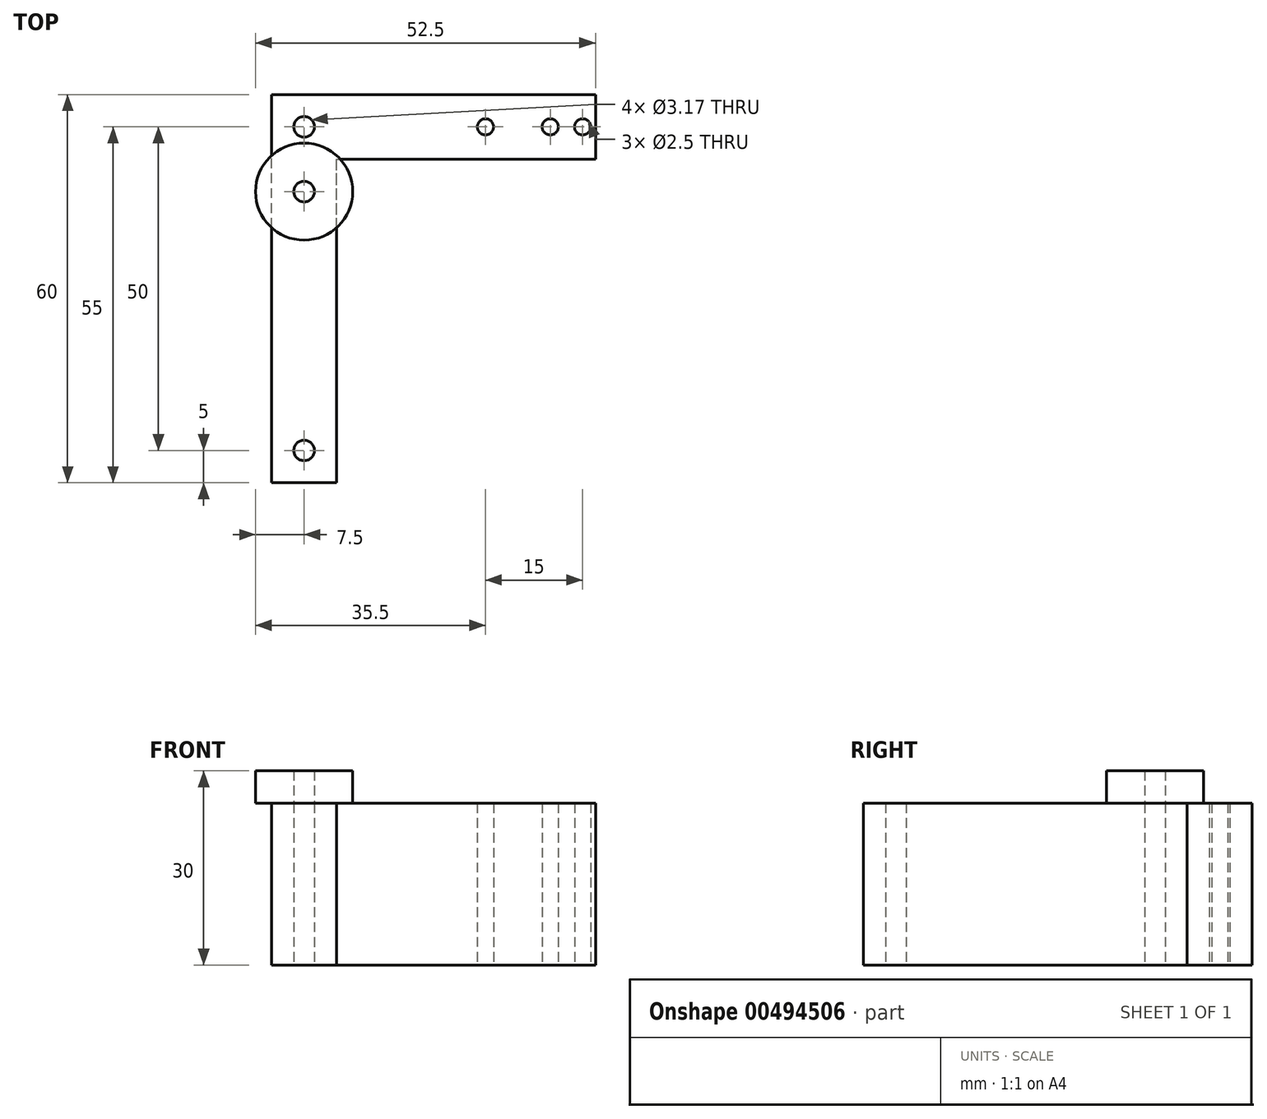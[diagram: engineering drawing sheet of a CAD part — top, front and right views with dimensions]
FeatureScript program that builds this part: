
annotation { "Feature Type Name" : "Feature", "Feature Type Description" : "" }
export const myFeature = defineFeature(function(context is Context, id is Id, definition is map)
    precondition{}
    {
        {
            var Q0;
            Q0=qCreatedBy(makeId("Top.planeOp"),FACE);
            var sketch = newSketch(context, id + "F0", { "sketchPlane" : qUnion([Q0])});
            skLineSegment(sketch, "E0.bottom", {"start": v(5, -30) * mm, "end": v(-5, -30) * mm});
            skLineSegment(sketch, "E0.top", {"start": v(5, 30) * mm, "end": v(-5, 30) * mm});
            skLineSegment(sketch, "E0.left", {"start": v(5, -30) * mm, "end": v(5, 30) * mm});
            skLineSegment(sketch, "E0.right", {"start": v(-5, -30) * mm, "end": v(-5, 30) * mm});
            skPoint(sketch, "E0.middle", {"position": v(0, 0) * mm});
            skCircle(sketch, "E1", {"center": v(0, 15) * mm, "radius": 1.59 * mm});
            skLineSegment(sketch, "E2.left", {"start": v(5, 0) * mm, "end": v(5, 30) * mm});
            skCircle(sketch, "E3", {"center": v(0, -25) * mm, "radius": 1.59 * mm});
            skCircle(sketch, "E4", {"center": v(0, 25) * mm, "radius": 1.59 * mm});
            skLineSegment(sketch, "E5.bottom", {"start": v(5, 30) * mm, "end": v(45, 30) * mm});
            skLineSegment(sketch, "E5.top", {"start": v(5, 20) * mm, "end": v(45, 20) * mm});
            skLineSegment(sketch, "E5.left", {"start": v(5, 30) * mm, "end": v(5, 20) * mm});
            skLineSegment(sketch, "E5.right", {"start": v(45, 30) * mm, "end": v(45, 20) * mm});
            skCircle(sketch, "E6", {"center": v(43, 25) * mm, "radius": 1.25 * mm});
            skPoint(sketch, "E6.centerSnap0", {"position": v(45, 25) * mm});
            skCircle(sketch, "E7", {"center": v(28, 25) * mm, "radius": 1.25 * mm});
            skCircle(sketch, "E8", {"center": v(38, 25) * mm, "radius": 1.25 * mm});
            skSolve(sketch);
        }
        {
            var Q0;
            Q0=makeQuery(id+"F0.imprint","IMPRINT",FACE,{"disambiguationData":[TD([[makeQuery(id+"F0.imprint","IMPRINT",EDGE,{"derivedFrom":sQuery(id+"F0.wireOp",EDGE,"E0.bottom")}),-1.0]])]});
            var Q1;
            Q1=makeQuery(id+"F0.imprint","IMPRINT",FACE,{"disambiguationData":[TD([[makeQuery(id+"F0.imprint","IMPRINT",EDGE,{"derivedFrom":sQuery(id+"F0.wireOp",EDGE,"E5.bottom")}),-1.0]])]});
            extrude(context, id + "F1", {"entities" : qUnion([Q0, Q1]), "depth" : 25 * mm, "offsetDistance" : 25 * mm});
        }
        {
            var Q0;
            Q0=makeQuery(id+"F1.opExtrude","CAP_FACE",FACE,{"disambiguationData":[OSD([sQuery(id+"F0.wireOp",EDGE,"E0.bottom"),sQuery(id+"F0.wireOp",EDGE,"E0.top"),sQuery(id+"F0.wireOp",EDGE,"E0.left"),sQuery(id+"F0.wireOp",EDGE,"E0.right"),sQuery(id+"F0.wireOp",EDGE,"E1"),sQuery(id+"F0.wireOp",EDGE,"E2.left"),sQuery(id+"F0.wireOp",EDGE,"E3"),sQuery(id+"F0.wireOp",EDGE,"E4"),sQuery(id+"F0.wireOp",EDGE,"E5.bottom"),sQuery(id+"F0.wireOp",EDGE,"E5.top"),sQuery(id+"F0.wireOp",EDGE,"E5.right"),sQuery(id+"F0.wireOp",EDGE,"E6"),sQuery(id+"F0.wireOp",EDGE,"E7"),sQuery(id+"F0.wireOp",EDGE,"E8")])],"isStart":false});
            var sketch = newSketch(context, id + "F2", { "sketchPlane" : qUnion([Q0])});
            skCircle(sketch, "E9", {"center": v(0, 15) * mm, "radius": 7.5 * mm});
            skCircle(sketch, "E10", {"center": v(0, 15) * mm, "radius": 1.59 * mm});
            skSolve(sketch);
        }
        {
            var Q0;
            Q0 = qSketchRegion(id + "F2", true);
            extrude(context, id + "F3", {"entities" : qUnion([Q0]), "depth" : 5 * mm, "offsetDistance" : 25 * mm});
        }
    });
